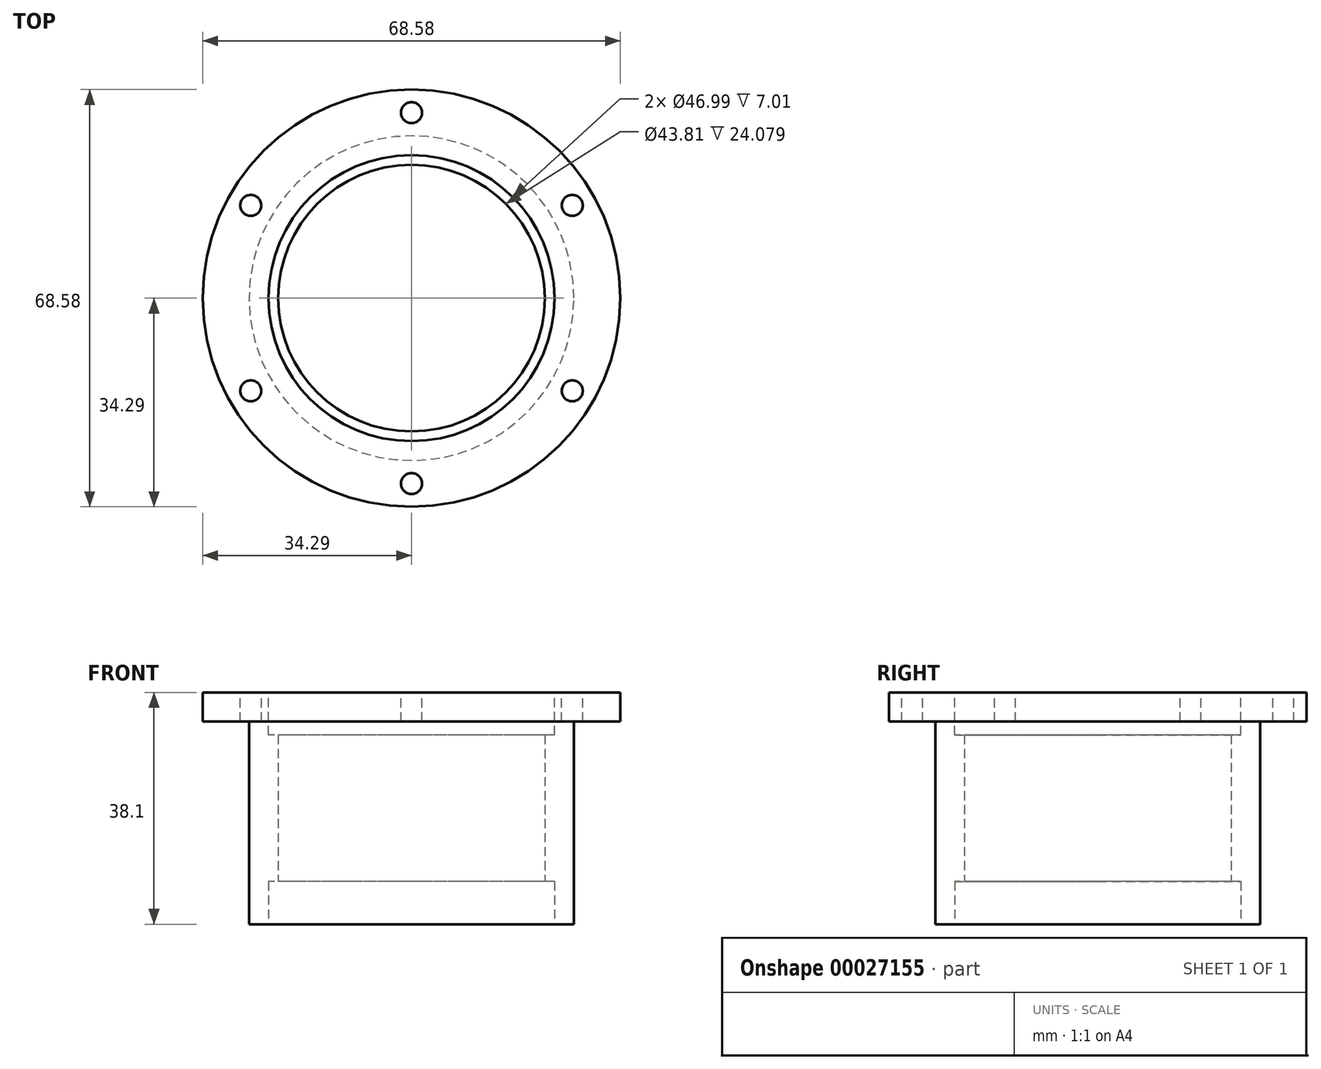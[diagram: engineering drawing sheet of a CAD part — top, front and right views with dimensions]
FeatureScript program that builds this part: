
annotation { "Feature Type Name" : "Feature", "Feature Type Description" : "" }
export const myFeature = defineFeature(function(context is Context, id is Id, definition is map)
    precondition{}
    {
        {
            var Q0;
            Q0=qCreatedBy(makeId("Top.planeOp"),FACE);
            var sketch = newSketch(context, id + "F0", { "sketchPlane" : qUnion([Q0])});
            skCircle(sketch, "E0", {"center": v(0, 0) * mm, "radius": 34.3 * mm});
            skCircle(sketch, "E1", {"center": v(0, 0) * mm, "radius": 26.67 * mm});
            skSolve(sketch);
        }
        {
            var Q0;
            Q0=makeQuery(id+"F0.imprint","IMPRINT",FACE,{"disambiguationData":[TD([[makeQuery(id+"F0.imprint","IMPRINT",EDGE,{"derivedFrom":sQuery(id+"F0.wireOp",EDGE,"E0")}),1.0]])]});
            var Q1;
            Q1=makeQuery(id+"F0.imprint","IMPRINT",FACE,{"disambiguationData":[TD([[makeQuery(id+"F0.imprint","IMPRINT",EDGE,{"derivedFrom":sQuery(id+"F0.wireOp",EDGE,"E1")}),1.0]])]});
            extrude(context, id + "F1", {"entities" : qUnion([Q0, Q1]), "depth" : 38.1 * mm});
        }
        {
            var Q0;
            Q0=makeQuery(id+"F1.opExtrude","CAP_FACE",FACE,{"disambiguationData":[OSD([sQuery(id+"F0.wireOp",EDGE,"E0")])],"isStart":false});
            var sketch = newSketch(context, id + "F2", { "sketchPlane" : qUnion([Q0])});
            skCircle(sketch, "E2", {"center": v(0, 0) * mm, "radius": 23.5 * mm});
            skSolve(sketch);
        }
        {
            var Q0;
            Q0=makeQuery(id+"F2.imprint","IMPRINT",FACE,{"disambiguationData":[TD([[makeQuery(id+"F2.imprint","IMPRINT",EDGE,{"derivedFrom":sQuery(id+"F2.wireOp",EDGE,"E2")}),1.0]])]});
            extrude(context, id + "F3", {"entities" : qUnion([Q0]), "operationType" : NewBodyOperationType.REMOVE, "oppositeDirection" : true, "depth" : 7 * mm});
        }
        {
            var Q0;
            Q0=makeQuery(id+"F1.opExtrude","CAP_FACE",FACE,{"disambiguationData":[OSD([sQuery(id+"F0.wireOp",EDGE,"E0")])],"isStart":true});
            var sketch = newSketch(context, id + "F4", { "sketchPlane" : qUnion([Q0])});
            skCircle(sketch, "E3", {"center": v(0, 0) * mm, "radius": 26.67 * mm});
            skSolve(sketch);
        }
        {
            var Q0;
            Q0=makeQuery(id+"F4.imprint","IMPRINT",FACE,{"disambiguationData":[TD([[makeQuery(id+"F4.imprint","IMPRINT",EDGE,{"derivedFrom":sQuery(id+"F4.wireOp",EDGE,"E3")}),-1.0]])]});
            extrude(context, id + "F5", {"entities" : qUnion([Q0]), "operationType" : NewBodyOperationType.REMOVE, "oppositeDirection" : true, "depth" : 33.32 * mm});
        }
        {
            var Q0;
            Q0=qCreatedBy(makeId("Top.planeOp"),FACE);
            var sketch = newSketch(context, id + "F6", { "sketchPlane" : qUnion([Q0])});
            skCircle(sketch, "E4", {"center": v(0, 0) * mm, "radius": 21.9 * mm});
            skCircle(sketch, "E5", {"center": v(0, 0) * mm, "radius": 23.5 * mm});
            skSolve(sketch);
        }
        {
            var Q0;
            Q0=makeQuery(id+"F6.imprint","IMPRINT",FACE,{"disambiguationData":[TD([[makeQuery(id+"F6.imprint","IMPRINT",EDGE,{"derivedFrom":sQuery(id+"F6.wireOp",EDGE,"E4")}),-1.0]])]});
            extrude(context, id + "F7", {"entities" : qUnion([Q0]), "operationType" : NewBodyOperationType.REMOVE, "depth" : 7 * mm});
        }
        {
            var Q0;
            Q0 = qSketchRegion(id + "F6", true);
            var Q1;
            Q1=makeQuery(id+"F7.boolean.opBoolean","SPLIT",FACE,{"disambiguationData":[TD([makeQuery(id+"F7.opExtrude","SWEPT_FACE",FACE,{"disambiguationData":[OSD([sQuery(id+"F6.wireOp",EDGE,"E4")])]})])],"derivedFrom":makeQuery(id+"F1.opExtrude","CAP_FACE",FACE,{"disambiguationData":[OSD([sQuery(id+"F0.wireOp",EDGE,"E0")])],"isStart":true})});
            extrude(context, id + "F8", {"entities" : qUnion([Q0, Q1]), "operationType" : NewBodyOperationType.REMOVE, "endBound" : BoundingType.THROUGH_ALL, "oppositeDirection" : true, "depth" : 25.4 * mm});
        }
        {
            var Q0;
            Q0=makeQuery(id+"F7.boolean.opBoolean","SPLIT",FACE,{"disambiguationData":[TD([makeQuery(id+"F7.opExtrude","SWEPT_FACE",FACE,{"disambiguationData":[OSD([sQuery(id+"F6.wireOp",EDGE,"E4")])]})])],"derivedFrom":makeQuery(id+"F1.opExtrude","CAP_FACE",FACE,{"disambiguationData":[OSD([sQuery(id+"F0.wireOp",EDGE,"E0")])],"isStart":true})});
            var sketch = newSketch(context, id + "F9", { "sketchPlane" : qUnion([Q0])});
            skCircle(sketch, "E6", {"center": v(0, 0) * mm, "radius": 21.9 * mm});
            skSolve(sketch);
        }
        {
            var Q0;
            Q0=makeQuery(id+"F9.imprint","IMPRINT",FACE,{"disambiguationData":[TD([[makeQuery(id+"F9.imprint","IMPRINT",EDGE,{"derivedFrom":sQuery(id+"F9.wireOp",EDGE,"E6")}),-1.0]])]});
            extrude(context, id + "F10", {"entities" : qUnion([Q0]), "operationType" : NewBodyOperationType.REMOVE, "endBound" : BoundingType.THROUGH_ALL, "oppositeDirection" : true, "depth" : 25.4 * mm});
        }
        {
            var Q0;
            Q0=makeQuery(id+"F1.opExtrude","CAP_FACE",FACE,{"disambiguationData":[OSD([sQuery(id+"F0.wireOp",EDGE,"E0")])],"isStart":false});
            var sketch = newSketch(context, id + "F11", { "sketchPlane" : qUnion([Q0])});
            skCircle(sketch, "E7", {"center": v(0, 0) * mm, "radius": 30.48 * mm});
            skCircle(sketch, "E8.cCircle", {"center": v(0, 0) * mm, "radius": 30.48 * mm, "construction": true});
            skLineSegment(sketch, "E8.0", {"start": v(0, 30.48) * mm, "end": v(26.4, 15.24) * mm});
            skLineSegment(sketch, "E8.1", {"start": v(26.4, 15.24) * mm, "end": v(26.4, -15.24) * mm});
            skLineSegment(sketch, "E8.2", {"start": v(26.4, -15.24) * mm, "end": v(0, -30.48) * mm});
            skLineSegment(sketch, "E8.3", {"start": v(0, -30.48) * mm, "end": v(-26.4, -15.24) * mm});
            skLineSegment(sketch, "E8.4", {"start": v(-26.4, -15.24) * mm, "end": v(-26.4, 15.24) * mm});
            skLineSegment(sketch, "E8.5", {"start": v(-26.4, 15.24) * mm, "end": v(0, 30.48) * mm});
            skCircle(sketch, "E9", {"center": v(0, 30.48) * mm, "radius": 1.73 * mm});
            skCircle(sketch, "E10", {"center": v(26.4, 15.24) * mm, "radius": 1.73 * mm});
            skCircle(sketch, "E11", {"center": v(26.4, -15.24) * mm, "radius": 1.73 * mm});
            skCircle(sketch, "E12", {"center": v(0, -30.48) * mm, "radius": 1.73 * mm});
            skCircle(sketch, "E13", {"center": v(-26.4, -15.24) * mm, "radius": 1.73 * mm});
            skCircle(sketch, "E14", {"center": v(-26.4, 15.24) * mm, "radius": 1.73 * mm});
            skSolve(sketch);
        }
        {
            var Q0;
            {var subQ0=sQuery(id+"F11.wireOp",EDGE,"E14");var subQ3=sQuery(id+"F11.wireOp",EDGE,"E8.4");var subQ4=makeQuery(id+"F11.imprint","INTERSECT",VERTEX,{"derivedFrom":[subQ3,subQ0]});Q0=makeQuery(id+"F11.imprint","IMPRINT",FACE,{"disambiguationData":[TD([[makeQuery(id+"F11.imprint","IMPRINT",EDGE,{"disambiguationData":[TD([[subQ4,-1.0]])],"derivedFrom":subQ0}),1.0]])]});}
            var Q1;
            {var subQ0=sQuery(id+"F11.wireOp",EDGE,"E14");var subQ3=sQuery(id+"F11.wireOp",EDGE,"E7");var subQ4=makeQuery(id+"F11.imprint","INTERSECT",VERTEX,{"disambiguationData":[OD(0.0)],"derivedFrom":[subQ3,subQ0]});Q1=makeQuery(id+"F11.imprint","IMPRINT",FACE,{"disambiguationData":[TD([[makeQuery(id+"F11.imprint","IMPRINT",EDGE,{"disambiguationData":[TD([[subQ4,1.0]])],"derivedFrom":subQ0}),1.0]])]});}
            var Q2;
            {var subQ0=sQuery(id+"F11.wireOp",EDGE,"E14");var subQ1=sQuery(id+"F11.wireOp",EDGE,"E7");var subQ3=makeQuery(id+"F11.imprint","INTERSECT",VERTEX,{"disambiguationData":[OD(0.0)],"derivedFrom":[subQ1,subQ0]});Q2=makeQuery(id+"F11.imprint","IMPRINT",FACE,{"disambiguationData":[TD([[makeQuery(id+"F11.imprint","IMPRINT",EDGE,{"disambiguationData":[TD([[subQ3,-1.0]])],"derivedFrom":subQ0}),1.0]])]});}
            var Q3;
            {var subQ0=sQuery(id+"F11.wireOp",EDGE,"E14");var subQ3=sQuery(id+"F11.wireOp",EDGE,"E7");var subQ4=makeQuery(id+"F11.imprint","INTERSECT",VERTEX,{"disambiguationData":[OD(1.0)],"derivedFrom":[subQ3,subQ0]});Q3=makeQuery(id+"F11.imprint","IMPRINT",FACE,{"disambiguationData":[TD([[makeQuery(id+"F11.imprint","IMPRINT",EDGE,{"disambiguationData":[TD([[subQ4,-1.0]])],"derivedFrom":subQ0}),1.0]])]});}
            var Q4;
            {var subQ0=sQuery(id+"F11.wireOp",EDGE,"E13");var subQ3=sQuery(id+"F11.wireOp",EDGE,"E8.3");var subQ4=makeQuery(id+"F11.imprint","INTERSECT",VERTEX,{"derivedFrom":[subQ3,subQ0]});Q4=makeQuery(id+"F11.imprint","IMPRINT",FACE,{"disambiguationData":[TD([[makeQuery(id+"F11.imprint","IMPRINT",EDGE,{"disambiguationData":[TD([[subQ4,-1.0]])],"derivedFrom":subQ0}),1.0]])]});}
            var Q5;
            {var subQ0=sQuery(id+"F11.wireOp",EDGE,"E13");var subQ3=sQuery(id+"F11.wireOp",EDGE,"E7");var subQ4=makeQuery(id+"F11.imprint","INTERSECT",VERTEX,{"disambiguationData":[OD(0.0)],"derivedFrom":[subQ3,subQ0]});Q5=makeQuery(id+"F11.imprint","IMPRINT",FACE,{"disambiguationData":[TD([[makeQuery(id+"F11.imprint","IMPRINT",EDGE,{"disambiguationData":[TD([[subQ4,1.0]])],"derivedFrom":subQ0}),1.0]])]});}
            var Q6;
            {var subQ0=sQuery(id+"F11.wireOp",EDGE,"E13");var subQ1=sQuery(id+"F11.wireOp",EDGE,"E7");var subQ3=makeQuery(id+"F11.imprint","INTERSECT",VERTEX,{"disambiguationData":[OD(0.0)],"derivedFrom":[subQ1,subQ0]});Q6=makeQuery(id+"F11.imprint","IMPRINT",FACE,{"disambiguationData":[TD([[makeQuery(id+"F11.imprint","IMPRINT",EDGE,{"disambiguationData":[TD([[subQ3,-1.0]])],"derivedFrom":subQ0}),1.0]])]});}
            var Q7;
            {var subQ0=sQuery(id+"F11.wireOp",EDGE,"E13");var subQ3=sQuery(id+"F11.wireOp",EDGE,"E7");var subQ4=makeQuery(id+"F11.imprint","INTERSECT",VERTEX,{"disambiguationData":[OD(1.0)],"derivedFrom":[subQ3,subQ0]});Q7=makeQuery(id+"F11.imprint","IMPRINT",FACE,{"disambiguationData":[TD([[makeQuery(id+"F11.imprint","IMPRINT",EDGE,{"disambiguationData":[TD([[subQ4,-1.0]])],"derivedFrom":subQ0}),1.0]])]});}
            var Q8;
            {var subQ0=sQuery(id+"F11.wireOp",EDGE,"E12");var subQ1=sQuery(id+"F11.wireOp",EDGE,"E7");var subQ3=makeQuery(id+"F11.imprint","INTERSECT",VERTEX,{"disambiguationData":[OD(0.0)],"derivedFrom":[subQ1,subQ0]});Q8=makeQuery(id+"F11.imprint","IMPRINT",FACE,{"disambiguationData":[TD([[makeQuery(id+"F11.imprint","IMPRINT",EDGE,{"disambiguationData":[TD([[subQ3,-1.0]])],"derivedFrom":subQ0}),1.0]])]});}
            var Q9;
            {var subQ0=sQuery(id+"F11.wireOp",EDGE,"E12");var subQ3=sQuery(id+"F11.wireOp",EDGE,"E8.2");var subQ4=makeQuery(id+"F11.imprint","INTERSECT",VERTEX,{"derivedFrom":[subQ3,subQ0]});Q9=makeQuery(id+"F11.imprint","IMPRINT",FACE,{"disambiguationData":[TD([[makeQuery(id+"F11.imprint","IMPRINT",EDGE,{"disambiguationData":[TD([[subQ4,-1.0]])],"derivedFrom":subQ0}),1.0]])]});}
            var Q10;
            {var subQ0=sQuery(id+"F11.wireOp",EDGE,"E12");var subQ3=sQuery(id+"F11.wireOp",EDGE,"E7");var subQ4=makeQuery(id+"F11.imprint","INTERSECT",VERTEX,{"disambiguationData":[OD(0.0)],"derivedFrom":[subQ3,subQ0]});Q10=makeQuery(id+"F11.imprint","IMPRINT",FACE,{"disambiguationData":[TD([[makeQuery(id+"F11.imprint","IMPRINT",EDGE,{"disambiguationData":[TD([[subQ4,1.0]])],"derivedFrom":subQ0}),1.0]])]});}
            var Q11;
            {var subQ1=sQuery(id+"F11.wireOp",EDGE,"E12");var subQ3=sQuery(id+"F11.wireOp",EDGE,"E7");var subQ5=makeQuery(id+"F11.imprint","INTERSECT",VERTEX,{"disambiguationData":[OD(1.0)],"derivedFrom":[subQ3,subQ1]});Q11=makeQuery(id+"F11.imprint","IMPRINT",FACE,{"disambiguationData":[TD([[makeQuery(id+"F11.imprint","IMPRINT",EDGE,{"disambiguationData":[TD([[subQ5,-1.0]])],"derivedFrom":subQ1}),1.0]])]});}
            var Q12;
            {var subQ1=sQuery(id+"F11.wireOp",EDGE,"E11");var subQ3=sQuery(id+"F11.wireOp",EDGE,"E7");var subQ5=makeQuery(id+"F11.imprint","INTERSECT",VERTEX,{"disambiguationData":[OD(0.0)],"derivedFrom":[subQ3,subQ1]});Q12=makeQuery(id+"F11.imprint","IMPRINT",FACE,{"disambiguationData":[TD([[makeQuery(id+"F11.imprint","IMPRINT",EDGE,{"disambiguationData":[TD([[subQ5,1.0]])],"derivedFrom":subQ1}),1.0]])]});}
            var Q13;
            {var subQ0=sQuery(id+"F11.wireOp",EDGE,"E11");var subQ3=sQuery(id+"F11.wireOp",EDGE,"E8.1");var subQ4=makeQuery(id+"F11.imprint","INTERSECT",VERTEX,{"derivedFrom":[subQ3,subQ0]});Q13=makeQuery(id+"F11.imprint","IMPRINT",FACE,{"disambiguationData":[TD([[makeQuery(id+"F11.imprint","IMPRINT",EDGE,{"disambiguationData":[TD([[subQ4,-1.0]])],"derivedFrom":subQ0}),1.0]])]});}
            var Q14;
            {var subQ0=sQuery(id+"F11.wireOp",EDGE,"E11");var subQ3=sQuery(id+"F11.wireOp",EDGE,"E7");var subQ4=makeQuery(id+"F11.imprint","INTERSECT",VERTEX,{"disambiguationData":[OD(1.0)],"derivedFrom":[subQ3,subQ0]});Q14=makeQuery(id+"F11.imprint","IMPRINT",FACE,{"disambiguationData":[TD([[makeQuery(id+"F11.imprint","IMPRINT",EDGE,{"disambiguationData":[TD([[subQ4,-1.0]])],"derivedFrom":subQ0}),1.0]])]});}
            var Q15;
            {var subQ0=sQuery(id+"F11.wireOp",EDGE,"E11");var subQ1=sQuery(id+"F11.wireOp",EDGE,"E7");var subQ3=makeQuery(id+"F11.imprint","INTERSECT",VERTEX,{"disambiguationData":[OD(0.0)],"derivedFrom":[subQ1,subQ0]});Q15=makeQuery(id+"F11.imprint","IMPRINT",FACE,{"disambiguationData":[TD([[makeQuery(id+"F11.imprint","IMPRINT",EDGE,{"disambiguationData":[TD([[subQ3,-1.0]])],"derivedFrom":subQ0}),1.0]])]});}
            var Q16;
            {var subQ0=sQuery(id+"F11.wireOp",EDGE,"E7");var subQ1=sQuery(id+"F11.wireOp",EDGE,"E10");var subQ4=makeQuery(id+"F11.imprint","INTERSECT",VERTEX,{"disambiguationData":[OD(0.0)],"derivedFrom":[subQ0,subQ1]});Q16=makeQuery(id+"F11.imprint","IMPRINT",FACE,{"disambiguationData":[TD([[makeQuery(id+"F11.imprint","IMPRINT",EDGE,{"disambiguationData":[TD([[subQ4,-1.0]])],"derivedFrom":subQ1}),1.0]])]});}
            var Q17;
            {var subQ0=sQuery(id+"F11.wireOp",EDGE,"E10");var subQ3=sQuery(id+"F11.wireOp",EDGE,"E7");var subQ4=makeQuery(id+"F11.imprint","INTERSECT",VERTEX,{"disambiguationData":[OD(1.0)],"derivedFrom":[subQ3,subQ0]});Q17=makeQuery(id+"F11.imprint","IMPRINT",FACE,{"disambiguationData":[TD([[makeQuery(id+"F11.imprint","IMPRINT",EDGE,{"disambiguationData":[TD([[subQ4,-1.0]])],"derivedFrom":subQ0}),1.0]])]});}
            var Q18;
            {var subQ0=sQuery(id+"F11.wireOp",EDGE,"E10");var subQ3=sQuery(id+"F11.wireOp",EDGE,"E8.0");var subQ4=makeQuery(id+"F11.imprint","INTERSECT",VERTEX,{"derivedFrom":[subQ3,subQ0]});Q18=makeQuery(id+"F11.imprint","IMPRINT",FACE,{"disambiguationData":[TD([[makeQuery(id+"F11.imprint","IMPRINT",EDGE,{"disambiguationData":[TD([[subQ4,-1.0]])],"derivedFrom":subQ0}),1.0]])]});}
            var Q19;
            {var subQ0=sQuery(id+"F11.wireOp",EDGE,"E10");var subQ3=sQuery(id+"F11.wireOp",EDGE,"E7");var subQ4=makeQuery(id+"F11.imprint","INTERSECT",VERTEX,{"disambiguationData":[OD(0.0)],"derivedFrom":[subQ3,subQ0]});Q19=makeQuery(id+"F11.imprint","IMPRINT",FACE,{"disambiguationData":[TD([[makeQuery(id+"F11.imprint","IMPRINT",EDGE,{"disambiguationData":[TD([[subQ4,1.0]])],"derivedFrom":subQ0}),1.0]])]});}
            var Q20;
            {var subQ0=sQuery(id+"F11.wireOp",EDGE,"E9");var subQ1=sQuery(id+"F11.wireOp",EDGE,"E7");var subQ3=makeQuery(id+"F11.imprint","INTERSECT",VERTEX,{"disambiguationData":[OD(0.0)],"derivedFrom":[subQ1,subQ0]});Q20=makeQuery(id+"F11.imprint","IMPRINT",FACE,{"disambiguationData":[TD([[makeQuery(id+"F11.imprint","IMPRINT",EDGE,{"disambiguationData":[TD([[subQ3,-1.0]])],"derivedFrom":subQ0}),1.0]])]});}
            var Q21;
            {var subQ0=sQuery(id+"F11.wireOp",EDGE,"E9");var subQ3=sQuery(id+"F11.wireOp",EDGE,"E8.0");var subQ4=makeQuery(id+"F11.imprint","INTERSECT",VERTEX,{"derivedFrom":[subQ3,subQ0]});Q21=makeQuery(id+"F11.imprint","IMPRINT",FACE,{"disambiguationData":[TD([[makeQuery(id+"F11.imprint","IMPRINT",EDGE,{"disambiguationData":[TD([[subQ4,1.0]])],"derivedFrom":subQ0}),1.0]])]});}
            var Q22;
            {var subQ0=sQuery(id+"F11.wireOp",EDGE,"E9");var subQ3=sQuery(id+"F11.wireOp",EDGE,"E7");var subQ4=makeQuery(id+"F11.imprint","INTERSECT",VERTEX,{"disambiguationData":[OD(1.0)],"derivedFrom":[subQ3,subQ0]});Q22=makeQuery(id+"F11.imprint","IMPRINT",FACE,{"disambiguationData":[TD([[makeQuery(id+"F11.imprint","IMPRINT",EDGE,{"disambiguationData":[TD([[subQ4,-1.0]])],"derivedFrom":subQ0}),1.0]])]});}
            var Q23;
            {var subQ0=sQuery(id+"F11.wireOp",EDGE,"E9");var subQ3=sQuery(id+"F11.wireOp",EDGE,"E7");var subQ4=makeQuery(id+"F11.imprint","INTERSECT",VERTEX,{"disambiguationData":[OD(0.0)],"derivedFrom":[subQ3,subQ0]});Q23=makeQuery(id+"F11.imprint","IMPRINT",FACE,{"disambiguationData":[TD([[makeQuery(id+"F11.imprint","IMPRINT",EDGE,{"disambiguationData":[TD([[subQ4,1.0]])],"derivedFrom":subQ0}),1.0]])]});}
            var Q24;
            Q24=makeQuery(id+"F5.boolean.opBoolean","COPY",FACE,{"derivedFrom":makeQuery(id+"F5.opExtrude","CAP_FACE",FACE,{"disambiguationData":[OSD([sQuery(id+"F0.wireOp",EDGE,"E0"),sQuery(id+"F4.wireOp",EDGE,"E3")])],"isStart":false})});
            extrude(context, id + "F12", {"entities" : qUnion([Q0, Q1, Q2, Q3, Q4, Q5, Q6, Q7, Q8, Q9, Q10, Q11, Q12, Q13, Q14, Q15, Q16, Q17, Q18, Q19, Q20, Q21, Q22, Q23]), "operationType" : NewBodyOperationType.REMOVE, "endBound" : BoundingType.UP_TO_SURFACE, "oppositeDirection" : true, "endBoundEntityFace" : qUnion([Q24]), "depth" : 25.4 * mm});
        }
    });
